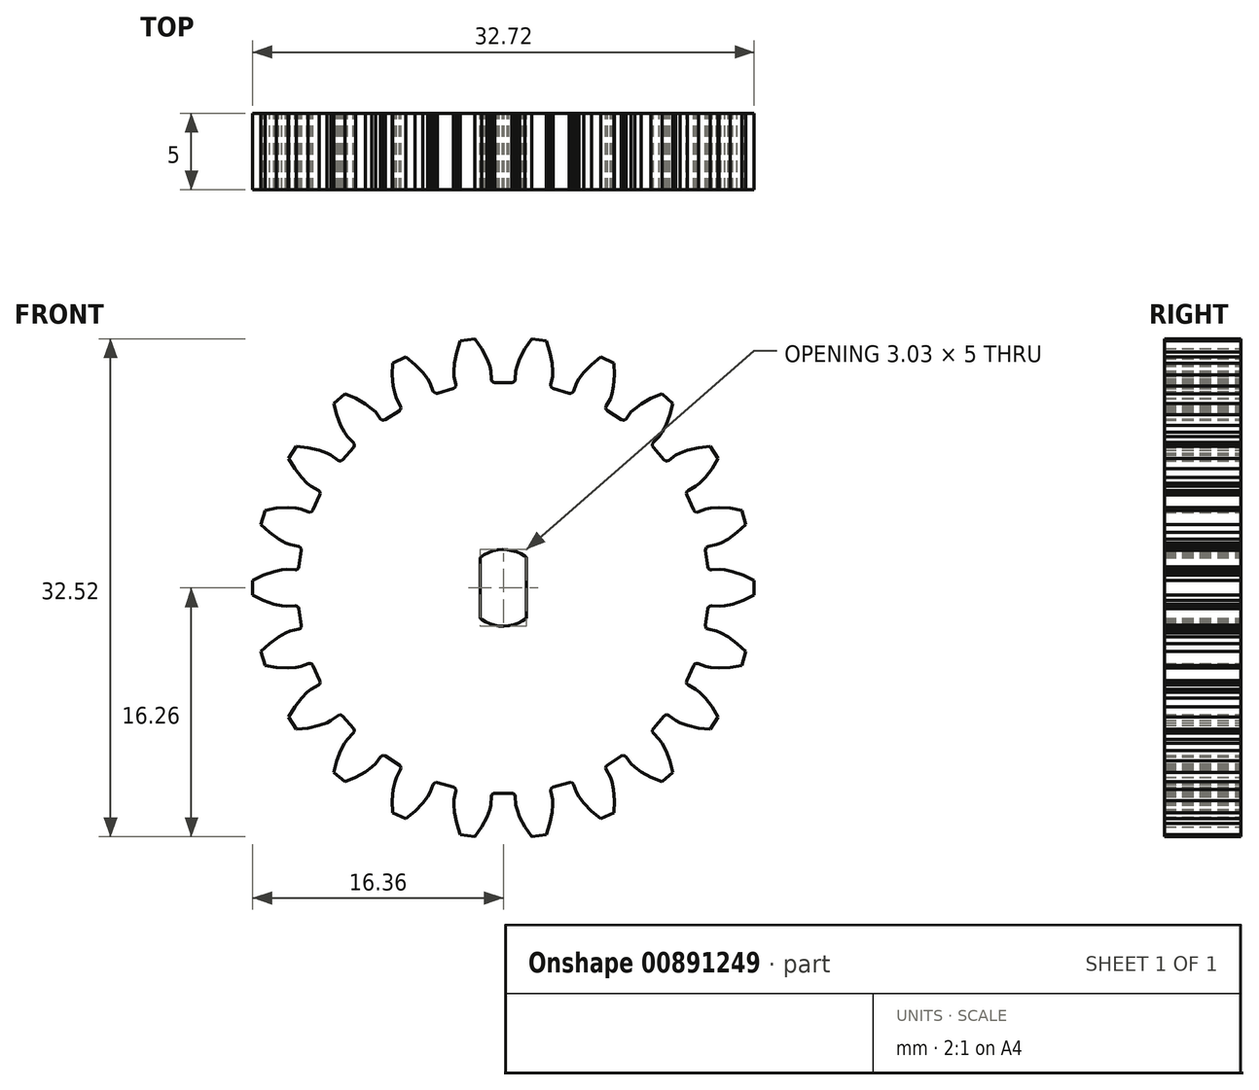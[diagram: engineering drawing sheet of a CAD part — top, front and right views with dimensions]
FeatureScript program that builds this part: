
annotation { "Feature Type Name" : "Feature", "Feature Type Description" : "" }
export const myFeature = defineFeature(function(context is Context, id is Id, definition is map)
    precondition{}
    {
        {
            var Q0;
            Q0=qCreatedBy(makeId("Front.planeOp"),FACE);
            var sketch = newSketch(context, id + "F0", { "sketchPlane" : qUnion([Q0])});
            skLineSegment(sketch, "E0", {"start": v(3.19, -14.67) * mm, "end": v(3.23, -14.15) * mm});
            skLineSegment(sketch, "E1", {"start": v(1.85, 16.26) * mm, "end": v(1.42, 15.62) * mm});
            skLineSegment(sketch, "E2", {"start": v(0.97, -2.3) * mm, "end": v(0.68, -2.4) * mm});
            skLineSegment(sketch, "E3", {"start": v(3.1, 13.28) * mm, "end": v(3.22, 13.83) * mm});
            skLineSegment(sketch, "E4", {"start": v(5.25, 14.06) * mm, "end": v(4.93, 13.65) * mm});
            skLineSegment(sketch, "E5", {"start": v(-9, -12.02) * mm, "end": v(-8.58, -11.7) * mm});
            skLineSegment(sketch, "E6", {"start": v(6.8, -11.58) * mm, "end": v(7.7, -10.99) * mm});
            skLineSegment(sketch, "E7", {"start": v(14.2, -2.94) * mm, "end": v(13.92, -2.82) * mm});
            skLineSegment(sketch, "E8", {"start": v(-0.54, 13.41) * mm, "end": v(-0.65, 13.44) * mm});
            skLineSegment(sketch, "E9", {"start": v(0.54, 13.41) * mm, "end": v(-0.54, 13.41) * mm});
            skLineSegment(sketch, "E10", {"start": v(-0.81, 14.18) * mm, "end": v(-0.89, 14.48) * mm});
            skLineSegment(sketch, "E11", {"start": v(-0.65, 13.44) * mm, "end": v(-0.74, 13.5) * mm});
            skLineSegment(sketch, "E12", {"start": v(-6.71, 11.66) * mm, "end": v(-6.8, 11.58) * mm});
            skLineSegment(sketch, "E13", {"start": v(0.81, 14.18) * mm, "end": v(0.77, 13.61) * mm});
            skLineSegment(sketch, "E14", {"start": v(-9.73, -9.3) * mm, "end": v(-9.73, -9.4) * mm});
            skLineSegment(sketch, "E15", {"start": v(3.1, 13.17) * mm, "end": v(3.1, 13.28) * mm});
            skLineSegment(sketch, "E16", {"start": v(-0.37, 2.47) * mm, "end": v(-0.06, 2.5) * mm});
            skLineSegment(sketch, "E17", {"start": v(0.68, -2.4) * mm, "end": v(0.37, -2.47) * mm});
            skLineSegment(sketch, "E18", {"start": v(4.57, 12.85) * mm, "end": v(4.51, 12.75) * mm});
            skLineSegment(sketch, "E19", {"start": v(0.89, 14.48) * mm, "end": v(0.81, 14.18) * mm});
            skLineSegment(sketch, "E20", {"start": v(1.25, -2.16) * mm, "end": v(0.97, -2.3) * mm});
            skLineSegment(sketch, "E21", {"start": v(-7.23, -14.68) * mm, "end": v(-6.36, -15.08) * mm});
            skLineSegment(sketch, "E22", {"start": v(-8.58, -11.7) * mm, "end": v(-8.35, -11.49) * mm});
            skLineSegment(sketch, "E23", {"start": v(-1.42, 15.62) * mm, "end": v(-1.85, 16.26) * mm});
            skLineSegment(sketch, "E24", {"start": v(0.37, -2.47) * mm, "end": v(0.06, -2.5) * mm});
            skLineSegment(sketch, "E25", {"start": v(-5.25, -14.06) * mm, "end": v(-4.93, -13.65) * mm});
            skLineSegment(sketch, "E26", {"start": v(3.04, 15.4) * mm, "end": v(2.8, 16.12) * mm});
            skLineSegment(sketch, "E27", {"start": v(-0.74, 13.5) * mm, "end": v(-0.77, 13.61) * mm});
            skLineSegment(sketch, "E28", {"start": v(14.07, -5.24) * mm, "end": v(14.8, -5.2) * mm});
            skLineSegment(sketch, "E29", {"start": v(-4.51, -12.75) * mm, "end": v(-4.41, -12.7) * mm});
            skLineSegment(sketch, "E30", {"start": v(-12.06, -6.36) * mm, "end": v(-12.56, -6.63) * mm});
            skLineSegment(sketch, "E31", {"start": v(-13.4, 1.27) * mm, "end": v(-13.48, 1.2) * mm});
            skLineSegment(sketch, "E32", {"start": v(-0.77, 13.61) * mm, "end": v(-0.81, 14.18) * mm});
            skLineSegment(sketch, "E33", {"start": v(-1.08, 14.97) * mm, "end": v(-1.42, 15.62) * mm});
            skLineSegment(sketch, "E34", {"start": v(-8, -11.04) * mm, "end": v(-7.92, -10.97) * mm});
            skLineSegment(sketch, "E35", {"start": v(-6.8, -11.58) * mm, "end": v(-6.71, -11.66) * mm});
            skLineSegment(sketch, "E36", {"start": v(-14.67, 3.2) * mm, "end": v(-14.2, 2.94) * mm});
            skLineSegment(sketch, "E37", {"start": v(-3.19, -14.67) * mm, "end": v(-3.04, -15.4) * mm});
            skLineSegment(sketch, "E38", {"start": v(0.54, -13.41) * mm, "end": v(0.65, -13.44) * mm});
            skLineSegment(sketch, "E39", {"start": v(-15.26, 3.63) * mm, "end": v(-14.67, 3.2) * mm});
            skLineSegment(sketch, "E40", {"start": v(-13.23, 5.15) * mm, "end": v(-13.54, 5.2) * mm});
            skLineSegment(sketch, "E41", {"start": v(-4.93, -13.65) * mm, "end": v(-4.77, -13.37) * mm});
            skLineSegment(sketch, "E42", {"start": v(-12.06, 6.36) * mm, "end": v(-11.98, 6.28) * mm});
            skLineSegment(sketch, "E43", {"start": v(-16.36, 0.48) * mm, "end": v(-16.36, -0.48) * mm});
            skLineSegment(sketch, "E44", {"start": v(-15.67, 0.82) * mm, "end": v(-16.36, 0.48) * mm});
            skLineSegment(sketch, "E45", {"start": v(3.19, 14.67) * mm, "end": v(3.04, 15.4) * mm});
            skLineSegment(sketch, "E46", {"start": v(3.23, 14.15) * mm, "end": v(3.19, 14.67) * mm});
            skLineSegment(sketch, "E47", {"start": v(3.22, 13.83) * mm, "end": v(3.23, 14.15) * mm});
            skLineSegment(sketch, "E48", {"start": v(0.26, 2.49) * mm, "end": v(0.57, 2.43) * mm});
            skLineSegment(sketch, "E49", {"start": v(-0.06, 2.5) * mm, "end": v(0.26, 2.49) * mm});
            skLineSegment(sketch, "E50", {"start": v(-14.02, -8.44) * mm, "end": v(-13.5, -9.25) * mm});
            skLineSegment(sketch, "E51", {"start": v(-13.62, -7.78) * mm, "end": v(-14.02, -8.44) * mm});
            skLineSegment(sketch, "E52", {"start": v(-0.68, 2.4) * mm, "end": v(-0.37, 2.47) * mm});
            skLineSegment(sketch, "E53", {"start": v(-3.16, 13.08) * mm, "end": v(-3.26, 13.02) * mm});
            skLineSegment(sketch, "E54", {"start": v(-3.1, 13.17) * mm, "end": v(-3.16, 13.08) * mm});
            skLineSegment(sketch, "E55", {"start": v(-3.1, 13.28) * mm, "end": v(-3.1, 13.17) * mm});
            skLineSegment(sketch, "E56", {"start": v(-3.22, 13.83) * mm, "end": v(-3.1, 13.28) * mm});
            skLineSegment(sketch, "E57", {"start": v(-3.23, 14.15) * mm, "end": v(-3.22, 13.83) * mm});
            skLineSegment(sketch, "E58", {"start": v(-3.19, 14.67) * mm, "end": v(-3.23, 14.15) * mm});
            skLineSegment(sketch, "E59", {"start": v(-3.04, 15.4) * mm, "end": v(-3.19, 14.67) * mm});
            skLineSegment(sketch, "E60", {"start": v(-2.8, 16.12) * mm, "end": v(-3.04, 15.4) * mm});
            skLineSegment(sketch, "E61", {"start": v(-1.85, 16.26) * mm, "end": v(-2.8, 16.12) * mm});
            skLineSegment(sketch, "E62", {"start": v(5.76, 14.6) * mm, "end": v(5.25, 14.06) * mm});
            skLineSegment(sketch, "E63", {"start": v(6.36, 15.08) * mm, "end": v(5.76, 14.6) * mm});
            skLineSegment(sketch, "E64", {"start": v(7.23, 14.68) * mm, "end": v(6.36, 15.08) * mm});
            skLineSegment(sketch, "E65", {"start": v(-7.2, 13.18) * mm, "end": v(-7.08, 12.66) * mm});
            skLineSegment(sketch, "E66", {"start": v(-7.25, 13.91) * mm, "end": v(-7.2, 13.18) * mm});
            skLineSegment(sketch, "E67", {"start": v(-7.23, 14.68) * mm, "end": v(-7.25, 13.91) * mm});
            skLineSegment(sketch, "E68", {"start": v(-6.36, 15.08) * mm, "end": v(-7.23, 14.68) * mm});
            skLineSegment(sketch, "E69", {"start": v(-5.76, 14.6) * mm, "end": v(-6.36, 15.08) * mm});
            skLineSegment(sketch, "E70", {"start": v(-5.25, 14.06) * mm, "end": v(-5.76, 14.6) * mm});
            skLineSegment(sketch, "E71", {"start": v(-4.93, 13.65) * mm, "end": v(-5.25, 14.06) * mm});
            skLineSegment(sketch, "E72", {"start": v(-4.77, 13.37) * mm, "end": v(-4.93, 13.65) * mm});
            skLineSegment(sketch, "E73", {"start": v(-4.57, 12.85) * mm, "end": v(-4.77, 13.37) * mm});
            skLineSegment(sketch, "E74", {"start": v(-4.51, 12.75) * mm, "end": v(-4.57, 12.85) * mm});
            skLineSegment(sketch, "E75", {"start": v(1.42, 15.62) * mm, "end": v(1.08, 14.97) * mm});
            skLineSegment(sketch, "E76", {"start": v(-13.54, 5.2) * mm, "end": v(-14.07, 5.24) * mm});
            skLineSegment(sketch, "E77", {"start": v(-0.89, 14.48) * mm, "end": v(-1.08, 14.97) * mm});
            skLineSegment(sketch, "E78", {"start": v(13.17, -7.2) * mm, "end": v(12.8, -6.82) * mm});
            skLineSegment(sketch, "E79", {"start": v(2.8, 16.12) * mm, "end": v(1.85, 16.26) * mm});
            skLineSegment(sketch, "E80", {"start": v(-2.8, -16.12) * mm, "end": v(-1.85, -16.26) * mm});
            skLineSegment(sketch, "E81", {"start": v(-11.97, -6.07) * mm, "end": v(-11.95, -6.17) * mm});
            skLineSegment(sketch, "E82", {"start": v(-6.71, -11.87) * mm, "end": v(-6.98, -12.36) * mm});
            skLineSegment(sketch, "E83", {"start": v(-14.46, 1.18) * mm, "end": v(-14.97, 1.07) * mm});
            skLineSegment(sketch, "E84", {"start": v(-14.07, 5.24) * mm, "end": v(-14.8, 5.2) * mm});
            skLineSegment(sketch, "E85", {"start": v(-1.85, -16.26) * mm, "end": v(-1.42, -15.62) * mm});
            skLineSegment(sketch, "E86", {"start": v(-6.36, -15.08) * mm, "end": v(-5.76, -14.6) * mm});
            skLineSegment(sketch, "E87", {"start": v(-4.3, -12.72) * mm, "end": v(-4.41, -12.7) * mm});
            skLineSegment(sketch, "E88", {"start": v(-7.7, -10.99) * mm, "end": v(-7.81, -10.95) * mm});
            skLineSegment(sketch, "E89", {"start": v(7.23, 14.68) * mm, "end": v(7.25, 13.91) * mm});
            skLineSegment(sketch, "E90", {"start": v(0.74, -13.5) * mm, "end": v(0.77, -13.61) * mm});
            skLineSegment(sketch, "E91", {"start": v(-15.56, 5.07) * mm, "end": v(-14.8, 5.2) * mm});
            skLineSegment(sketch, "E92", {"start": v(-3.22, -13.83) * mm, "end": v(-3.23, -14.15) * mm});
            skLineSegment(sketch, "E93", {"start": v(-15.56, 5.07) * mm, "end": v(-15.83, 4.15) * mm});
            skLineSegment(sketch, "E94", {"start": v(-12.8, -6.82) * mm, "end": v(-13.17, -7.2) * mm});
            skLineSegment(sketch, "E95", {"start": v(-13.23, 5.15) * mm, "end": v(-12.7, 4.96) * mm});
            skLineSegment(sketch, "E96", {"start": v(-5.25, -14.06) * mm, "end": v(-5.76, -14.6) * mm});
            skLineSegment(sketch, "E97", {"start": v(-15.26, 3.63) * mm, "end": v(-15.83, 4.15) * mm});
            skLineSegment(sketch, "E98", {"start": v(13.5, -9.25) * mm, "end": v(12.74, -9.16) * mm});
            skLineSegment(sketch, "E99", {"start": v(-13.2, -2.56) * mm, "end": v(-13.27, -2.65) * mm});
            skLineSegment(sketch, "E100", {"start": v(-12.8, -6.82) * mm, "end": v(-12.56, -6.63) * mm});
            skLineSegment(sketch, "E101", {"start": v(-13.48, -1.2) * mm, "end": v(-13.59, -1.18) * mm});
            skLineSegment(sketch, "E102", {"start": v(-3.16, -13.08) * mm, "end": v(-3.1, -13.17) * mm});
            skLineSegment(sketch, "E103", {"start": v(-0.89, -14.48) * mm, "end": v(-1.08, -14.97) * mm});
            skLineSegment(sketch, "E104", {"start": v(11.53, -8.81) * mm, "end": v(11.24, -8.67) * mm});
            skLineSegment(sketch, "E105", {"start": v(-12.02, -9) * mm, "end": v(-12.74, -9.16) * mm});
            skLineSegment(sketch, "E106", {"start": v(-7.81, -10.95) * mm, "end": v(-7.92, -10.97) * mm});
            skLineSegment(sketch, "E107", {"start": v(-0.54, -13.41) * mm, "end": v(-0.65, -13.44) * mm});
            skLineSegment(sketch, "E108", {"start": v(9.64, -12.38) * mm, "end": v(9, -12.02) * mm});
            skLineSegment(sketch, "E109", {"start": v(-3.1, -13.28) * mm, "end": v(-3.22, -13.83) * mm});
            skLineSegment(sketch, "E110", {"start": v(-3.04, -15.4) * mm, "end": v(-2.8, -16.12) * mm});
            skLineSegment(sketch, "E111", {"start": v(-1.5, -2) * mm, "end": v(-1.51, 1.99) * mm});
            skLineSegment(sketch, "E112", {"start": v(-1.42, -2.05) * mm, "end": v(-1.5, -2) * mm});
            skLineSegment(sketch, "E113", {"start": v(-1.16, -2.22) * mm, "end": v(-1.42, -2.05) * mm});
            skLineSegment(sketch, "E114", {"start": v(-1.42, -15.62) * mm, "end": v(-1.08, -14.97) * mm});
            skLineSegment(sketch, "E115", {"start": v(-0.87, -2.34) * mm, "end": v(-1.16, -2.22) * mm});
            skLineSegment(sketch, "E116", {"start": v(-0.89, -14.48) * mm, "end": v(-0.81, -14.18) * mm});
            skLineSegment(sketch, "E117", {"start": v(-0.57, -2.43) * mm, "end": v(-0.87, -2.34) * mm});
            skLineSegment(sketch, "E118", {"start": v(-0.81, -14.18) * mm, "end": v(-0.77, -13.61) * mm});
            skLineSegment(sketch, "E119", {"start": v(-0.77, -13.61) * mm, "end": v(-0.74, -13.5) * mm});
            skLineSegment(sketch, "E120", {"start": v(-0.74, -13.5) * mm, "end": v(-0.65, -13.44) * mm});
            skLineSegment(sketch, "E121", {"start": v(-0.26, -2.49) * mm, "end": v(-0.57, -2.43) * mm});
            skLineSegment(sketch, "E122", {"start": v(-0.54, -13.41) * mm, "end": v(0.54, -13.41) * mm});
            skLineSegment(sketch, "E123", {"start": v(0.06, -2.5) * mm, "end": v(-0.26, -2.49) * mm});
            skLineSegment(sketch, "E124", {"start": v(0.65, -13.44) * mm, "end": v(0.74, -13.5) * mm});
            skLineSegment(sketch, "E125", {"start": v(0.77, -13.61) * mm, "end": v(0.81, -14.18) * mm});
            skLineSegment(sketch, "E126", {"start": v(0.81, -14.18) * mm, "end": v(0.89, -14.48) * mm});
            skLineSegment(sketch, "E127", {"start": v(0.89, -14.48) * mm, "end": v(1.08, -14.97) * mm});
            skLineSegment(sketch, "E128", {"start": v(1.08, -14.97) * mm, "end": v(1.42, -15.62) * mm});
            skLineSegment(sketch, "E129", {"start": v(1.51, -1.99) * mm, "end": v(1.25, -2.16) * mm});
            skLineSegment(sketch, "E130", {"start": v(1.42, -15.62) * mm, "end": v(1.85, -16.26) * mm});
            skLineSegment(sketch, "E131", {"start": v(-15.26, -3.63) * mm, "end": v(-15.83, -4.15) * mm});
            skLineSegment(sketch, "E132", {"start": v(-15.83, -4.15) * mm, "end": v(-15.56, -5.07) * mm});
            skLineSegment(sketch, "E133", {"start": v(-15.56, -5.07) * mm, "end": v(-14.8, -5.2) * mm});
            skLineSegment(sketch, "E134", {"start": v(-14.67, -3.2) * mm, "end": v(-15.26, -3.63) * mm});
            skLineSegment(sketch, "E135", {"start": v(-14.8, -5.2) * mm, "end": v(-14.07, -5.24) * mm});
            skLineSegment(sketch, "E136", {"start": v(-14.2, -2.94) * mm, "end": v(-14.67, -3.2) * mm});
            skLineSegment(sketch, "E137", {"start": v(-13.92, -2.82) * mm, "end": v(-14.2, -2.94) * mm});
            skLineSegment(sketch, "E138", {"start": v(-14.07, -5.24) * mm, "end": v(-13.54, -5.2) * mm});
            skLineSegment(sketch, "E139", {"start": v(-13.37, -2.7) * mm, "end": v(-13.92, -2.82) * mm});
            skLineSegment(sketch, "E140", {"start": v(-13.54, -5.2) * mm, "end": v(-13.23, -5.15) * mm});
            skLineSegment(sketch, "E141", {"start": v(-13.27, -2.65) * mm, "end": v(-13.37, -2.7) * mm});
            skLineSegment(sketch, "E142", {"start": v(-13.23, -5.15) * mm, "end": v(-12.7, -4.96) * mm});
            skLineSegment(sketch, "E143", {"start": v(-13.2, -2.45) * mm, "end": v(-13.2, -2.56) * mm});
            skLineSegment(sketch, "E144", {"start": v(-13.17, -7.2) * mm, "end": v(-13.62, -7.78) * mm});
            skLineSegment(sketch, "E145", {"start": v(-13.5, -9.25) * mm, "end": v(-12.74, -9.16) * mm});
            skLineSegment(sketch, "E146", {"start": v(-11.98, -6.28) * mm, "end": v(-12.06, -6.36) * mm});
            skLineSegment(sketch, "E147", {"start": v(-12.02, -9) * mm, "end": v(-11.53, -8.81) * mm});
            skLineSegment(sketch, "E148", {"start": v(-11.95, -6.17) * mm, "end": v(-11.98, -6.28) * mm});
            skLineSegment(sketch, "E149", {"start": v(-10.88, -11.3) * mm, "end": v(-11.08, -12.05) * mm});
            skLineSegment(sketch, "E150", {"start": v(-11.08, -12.05) * mm, "end": v(-10.35, -12.68) * mm});
            skLineSegment(sketch, "E151", {"start": v(-10.61, -10.62) * mm, "end": v(-10.88, -11.3) * mm});
            skLineSegment(sketch, "E152", {"start": v(-10.36, -10.15) * mm, "end": v(-10.61, -10.62) * mm});
            skLineSegment(sketch, "E153", {"start": v(-10.18, -9.9) * mm, "end": v(-10.36, -10.15) * mm});
            skLineSegment(sketch, "E154", {"start": v(-10.35, -12.68) * mm, "end": v(-9.64, -12.38) * mm});
            skLineSegment(sketch, "E155", {"start": v(-9.79, -9.5) * mm, "end": v(-10.18, -9.9) * mm});
            skLineSegment(sketch, "E156", {"start": v(-9.73, -9.4) * mm, "end": v(-9.79, -9.5) * mm});
            skLineSegment(sketch, "E157", {"start": v(-7.2, -13.18) * mm, "end": v(-7.25, -13.91) * mm});
            skLineSegment(sketch, "E158", {"start": v(-7.25, -13.91) * mm, "end": v(-7.23, -14.68) * mm});
            skLineSegment(sketch, "E159", {"start": v(-7.08, -12.66) * mm, "end": v(-7.2, -13.18) * mm});
            skLineSegment(sketch, "E160", {"start": v(-6.98, -12.36) * mm, "end": v(-7.08, -12.66) * mm});
            skLineSegment(sketch, "E161", {"start": v(-6.69, -11.76) * mm, "end": v(-6.71, -11.87) * mm});
            skLineSegment(sketch, "E162", {"start": v(-3.23, -14.15) * mm, "end": v(-3.19, -14.67) * mm});
            skLineSegment(sketch, "E163", {"start": v(-7.08, 12.66) * mm, "end": v(-6.98, 12.36) * mm});
            skLineSegment(sketch, "E164", {"start": v(-6.98, 12.36) * mm, "end": v(-6.71, 11.87) * mm});
            skLineSegment(sketch, "E165", {"start": v(-6.71, 11.87) * mm, "end": v(-6.69, 11.76) * mm});
            skLineSegment(sketch, "E166", {"start": v(-4.77, -13.37) * mm, "end": v(-4.57, -12.85) * mm});
            skLineSegment(sketch, "E167", {"start": v(-4.57, -12.85) * mm, "end": v(-4.51, -12.75) * mm});
            skLineSegment(sketch, "E168", {"start": v(-4.41, 12.7) * mm, "end": v(-4.51, 12.75) * mm});
            skLineSegment(sketch, "E169", {"start": v(-4.3, 12.72) * mm, "end": v(-4.41, 12.7) * mm});
            skLineSegment(sketch, "E170", {"start": v(-4.3, -12.72) * mm, "end": v(-3.26, -13.02) * mm});
            skLineSegment(sketch, "E171", {"start": v(-3.26, 13.02) * mm, "end": v(-4.3, 12.72) * mm});
            skLineSegment(sketch, "E172", {"start": v(-3.26, -13.02) * mm, "end": v(-3.16, -13.08) * mm});
            skLineSegment(sketch, "E173", {"start": v(-3.1, -13.17) * mm, "end": v(-3.1, -13.28) * mm});
            skLineSegment(sketch, "E174", {"start": v(-10.35, 12.68) * mm, "end": v(-11.08, 12.05) * mm});
            skLineSegment(sketch, "E175", {"start": v(-11.08, 12.05) * mm, "end": v(-10.88, 11.3) * mm});
            skLineSegment(sketch, "E176", {"start": v(-10.88, 11.3) * mm, "end": v(-10.61, 10.62) * mm});
            skLineSegment(sketch, "E177", {"start": v(-10.61, 10.62) * mm, "end": v(-10.36, 10.15) * mm});
            skLineSegment(sketch, "E178", {"start": v(-10.36, 10.15) * mm, "end": v(-10.18, 9.9) * mm});
            skLineSegment(sketch, "E179", {"start": v(-9.64, 12.38) * mm, "end": v(-10.35, 12.68) * mm});
            skLineSegment(sketch, "E180", {"start": v(-10.18, 9.9) * mm, "end": v(-9.79, 9.5) * mm});
            skLineSegment(sketch, "E181", {"start": v(-9.79, 9.5) * mm, "end": v(-9.73, 9.4) * mm});
            skLineSegment(sketch, "E182", {"start": v(-9.73, 9.4) * mm, "end": v(-9.73, 9.3) * mm});
            skLineSegment(sketch, "E183", {"start": v(-9.64, -12.38) * mm, "end": v(-9, -12.02) * mm});
            skLineSegment(sketch, "E184", {"start": v(-9, 12.02) * mm, "end": v(-9.64, 12.38) * mm});
            skLineSegment(sketch, "E185", {"start": v(-8.58, 11.7) * mm, "end": v(-9, 12.02) * mm});
            skLineSegment(sketch, "E186", {"start": v(-8.35, 11.49) * mm, "end": v(-8.58, 11.7) * mm});
            skLineSegment(sketch, "E187", {"start": v(-8.35, -11.49) * mm, "end": v(-8, -11.04) * mm});
            skLineSegment(sketch, "E188", {"start": v(-8, 11.04) * mm, "end": v(-8.35, 11.49) * mm});
            skLineSegment(sketch, "E189", {"start": v(-7.92, 10.97) * mm, "end": v(-8, 11.04) * mm});
            skLineSegment(sketch, "E190", {"start": v(-7.81, 10.95) * mm, "end": v(-7.92, 10.97) * mm});
            skLineSegment(sketch, "E191", {"start": v(-7.7, 10.99) * mm, "end": v(-7.81, 10.95) * mm});
            skLineSegment(sketch, "E192", {"start": v(-7.7, -10.99) * mm, "end": v(-6.8, -11.58) * mm});
            skLineSegment(sketch, "E193", {"start": v(-6.8, 11.58) * mm, "end": v(-7.7, 10.99) * mm});
            skLineSegment(sketch, "E194", {"start": v(-6.71, -11.66) * mm, "end": v(-6.69, -11.76) * mm});
            skLineSegment(sketch, "E195", {"start": v(-6.69, 11.76) * mm, "end": v(-6.71, 11.66) * mm});
            skLineSegment(sketch, "E196", {"start": v(-13.5, 9.25) * mm, "end": v(-14.02, 8.44) * mm});
            skLineSegment(sketch, "E197", {"start": v(-14.02, 8.44) * mm, "end": v(-13.62, 7.78) * mm});
            skLineSegment(sketch, "E198", {"start": v(-13.62, 7.78) * mm, "end": v(-13.17, 7.2) * mm});
            skLineSegment(sketch, "E199", {"start": v(-12.74, 9.16) * mm, "end": v(-13.5, 9.25) * mm});
            skLineSegment(sketch, "E200", {"start": v(-13.17, 7.2) * mm, "end": v(-12.8, 6.82) * mm});
            skLineSegment(sketch, "E201", {"start": v(-12.8, 6.82) * mm, "end": v(-12.56, 6.63) * mm});
            skLineSegment(sketch, "E202", {"start": v(-12.02, 9) * mm, "end": v(-12.74, 9.16) * mm});
            skLineSegment(sketch, "E203", {"start": v(-12.56, 6.63) * mm, "end": v(-12.06, 6.36) * mm});
            skLineSegment(sketch, "E204", {"start": v(-11.53, 8.81) * mm, "end": v(-12.02, 9) * mm});
            skLineSegment(sketch, "E205", {"start": v(-11.98, 6.28) * mm, "end": v(-11.95, 6.17) * mm});
            skLineSegment(sketch, "E206", {"start": v(-11.53, -8.81) * mm, "end": v(-11.24, -8.67) * mm});
            skLineSegment(sketch, "E207", {"start": v(-11.24, 8.67) * mm, "end": v(-11.53, 8.81) * mm});
            skLineSegment(sketch, "E208", {"start": v(-11.24, -8.67) * mm, "end": v(-10.8, -8.33) * mm});
            skLineSegment(sketch, "E209", {"start": v(-10.8, 8.33) * mm, "end": v(-11.24, 8.67) * mm});
            skLineSegment(sketch, "E210", {"start": v(-10.8, -8.33) * mm, "end": v(-10.7, -8.3) * mm});
            skLineSegment(sketch, "E211", {"start": v(-10.7, 8.3) * mm, "end": v(-10.8, 8.33) * mm});
            skLineSegment(sketch, "E212", {"start": v(-10.7, -8.3) * mm, "end": v(-10.58, -8.3) * mm});
            skLineSegment(sketch, "E213", {"start": v(-10.58, 8.3) * mm, "end": v(-10.7, 8.3) * mm});
            skLineSegment(sketch, "E214", {"start": v(-10.58, -8.3) * mm, "end": v(-10.5, -8.37) * mm});
            skLineSegment(sketch, "E215", {"start": v(-10.5, 8.37) * mm, "end": v(-10.58, 8.3) * mm});
            skLineSegment(sketch, "E216", {"start": v(-10.5, -8.37) * mm, "end": v(-9.78, -9.2) * mm});
            skLineSegment(sketch, "E217", {"start": v(-9.78, 9.2) * mm, "end": v(-10.5, 8.37) * mm});
            skLineSegment(sketch, "E218", {"start": v(-9.78, -9.2) * mm, "end": v(-9.73, -9.3) * mm});
            skLineSegment(sketch, "E219", {"start": v(-9.73, 9.3) * mm, "end": v(-9.78, 9.2) * mm});
            skLineSegment(sketch, "E220", {"start": v(-14.2, 2.94) * mm, "end": v(-13.92, 2.82) * mm});
            skLineSegment(sketch, "E221", {"start": v(-13.92, 2.82) * mm, "end": v(-13.37, 2.7) * mm});
            skLineSegment(sketch, "E222", {"start": v(-13.37, 2.7) * mm, "end": v(-13.27, 2.65) * mm});
            skLineSegment(sketch, "E223", {"start": v(-13.27, 2.65) * mm, "end": v(-13.2, 2.56) * mm});
            skLineSegment(sketch, "E224", {"start": v(-13.2, 2.56) * mm, "end": v(-13.2, 2.45) * mm});
            skLineSegment(sketch, "E225", {"start": v(-12.7, -4.96) * mm, "end": v(-12.6, -4.94) * mm});
            skLineSegment(sketch, "E226", {"start": v(-12.6, 4.94) * mm, "end": v(-12.7, 4.96) * mm});
            skLineSegment(sketch, "E227", {"start": v(-12.6, -4.94) * mm, "end": v(-12.5, -4.99) * mm});
            skLineSegment(sketch, "E228", {"start": v(-12.5, 4.99) * mm, "end": v(-12.6, 4.94) * mm});
            skLineSegment(sketch, "E229", {"start": v(-12.5, -4.99) * mm, "end": v(-12.43, -5.08) * mm});
            skLineSegment(sketch, "E230", {"start": v(-12.43, 5.08) * mm, "end": v(-12.5, 4.99) * mm});
            skLineSegment(sketch, "E231", {"start": v(-12.43, -5.08) * mm, "end": v(-11.97, -6.07) * mm});
            skLineSegment(sketch, "E232", {"start": v(-11.97, 6.07) * mm, "end": v(-12.43, 5.08) * mm});
            skLineSegment(sketch, "E233", {"start": v(-11.95, 6.17) * mm, "end": v(-11.97, 6.07) * mm});
            skLineSegment(sketch, "E234", {"start": v(-16.36, -0.48) * mm, "end": v(-15.67, -0.82) * mm});
            skLineSegment(sketch, "E235", {"start": v(-15.67, -0.82) * mm, "end": v(-14.97, -1.07) * mm});
            skLineSegment(sketch, "E236", {"start": v(-14.97, 1.07) * mm, "end": v(-15.67, 0.82) * mm});
            skLineSegment(sketch, "E237", {"start": v(-14.97, -1.07) * mm, "end": v(-14.46, -1.18) * mm});
            skLineSegment(sketch, "E238", {"start": v(-14.46, -1.18) * mm, "end": v(-14.15, -1.22) * mm});
            skLineSegment(sketch, "E239", {"start": v(-14.15, 1.22) * mm, "end": v(-14.46, 1.18) * mm});
            skLineSegment(sketch, "E240", {"start": v(-14.15, -1.22) * mm, "end": v(-13.59, -1.18) * mm});
            skLineSegment(sketch, "E241", {"start": v(-13.59, 1.18) * mm, "end": v(-14.15, 1.22) * mm});
            skLineSegment(sketch, "E242", {"start": v(-13.48, 1.2) * mm, "end": v(-13.59, 1.18) * mm});
            skLineSegment(sketch, "E243", {"start": v(-13.48, -1.2) * mm, "end": v(-13.4, -1.27) * mm});
            skLineSegment(sketch, "E244", {"start": v(-13.4, -1.27) * mm, "end": v(-13.35, -1.37) * mm});
            skLineSegment(sketch, "E245", {"start": v(-13.35, 1.37) * mm, "end": v(-13.4, 1.27) * mm});
            skLineSegment(sketch, "E246", {"start": v(-13.35, -1.37) * mm, "end": v(-13.2, -2.45) * mm});
            skLineSegment(sketch, "E247", {"start": v(-13.2, 2.45) * mm, "end": v(-13.35, 1.37) * mm});
            skLineSegment(sketch, "E248", {"start": v(-1.51, 1.99) * mm, "end": v(-1.25, 2.16) * mm});
            skLineSegment(sketch, "E249", {"start": v(-1.25, 2.16) * mm, "end": v(-0.97, 2.3) * mm});
            skLineSegment(sketch, "E250", {"start": v(-0.97, 2.3) * mm, "end": v(-0.68, 2.4) * mm});
            skLineSegment(sketch, "E251", {"start": v(0.65, 13.44) * mm, "end": v(0.54, 13.41) * mm});
            skLineSegment(sketch, "E252", {"start": v(0.57, 2.43) * mm, "end": v(0.87, 2.34) * mm});
            skLineSegment(sketch, "E253", {"start": v(0.74, 13.5) * mm, "end": v(0.65, 13.44) * mm});
            skLineSegment(sketch, "E254", {"start": v(0.77, 13.61) * mm, "end": v(0.74, 13.5) * mm});
            skLineSegment(sketch, "E255", {"start": v(0.87, 2.34) * mm, "end": v(1.16, 2.22) * mm});
            skLineSegment(sketch, "E256", {"start": v(1.08, 14.97) * mm, "end": v(0.89, 14.48) * mm});
            skLineSegment(sketch, "E257", {"start": v(1.16, 2.22) * mm, "end": v(1.42, 2.05) * mm});
            skLineSegment(sketch, "E258", {"start": v(1.42, 2.05) * mm, "end": v(1.5, 2) * mm});
            skLineSegment(sketch, "E259", {"start": v(1.5, 2) * mm, "end": v(1.51, -1.99) * mm});
            skLineSegment(sketch, "E260", {"start": v(1.85, -16.26) * mm, "end": v(2.8, -16.12) * mm});
            skLineSegment(sketch, "E261", {"start": v(2.8, -16.12) * mm, "end": v(3.04, -15.4) * mm});
            skLineSegment(sketch, "E262", {"start": v(3.04, -15.4) * mm, "end": v(3.19, -14.67) * mm});
            skLineSegment(sketch, "E263", {"start": v(3.22, -13.83) * mm, "end": v(3.1, -13.28) * mm});
            skLineSegment(sketch, "E264", {"start": v(3.23, -14.15) * mm, "end": v(3.22, -13.83) * mm});
            skLineSegment(sketch, "E265", {"start": v(3.1, -13.28) * mm, "end": v(3.1, -13.17) * mm});
            skLineSegment(sketch, "E266", {"start": v(3.1, -13.17) * mm, "end": v(3.16, -13.08) * mm});
            skLineSegment(sketch, "E267", {"start": v(3.16, 13.08) * mm, "end": v(3.1, 13.17) * mm});
            skLineSegment(sketch, "E268", {"start": v(3.16, -13.08) * mm, "end": v(3.26, -13.02) * mm});
            skLineSegment(sketch, "E269", {"start": v(3.26, 13.02) * mm, "end": v(3.16, 13.08) * mm});
            skLineSegment(sketch, "E270", {"start": v(3.26, -13.02) * mm, "end": v(4.3, -12.72) * mm});
            skLineSegment(sketch, "E271", {"start": v(4.3, 12.72) * mm, "end": v(3.26, 13.02) * mm});
            skLineSegment(sketch, "E272", {"start": v(4.3, -12.72) * mm, "end": v(4.41, -12.7) * mm});
            skLineSegment(sketch, "E273", {"start": v(4.41, 12.7) * mm, "end": v(4.3, 12.72) * mm});
            skLineSegment(sketch, "E274", {"start": v(4.41, -12.7) * mm, "end": v(4.51, -12.75) * mm});
            skLineSegment(sketch, "E275", {"start": v(4.51, 12.75) * mm, "end": v(4.41, 12.7) * mm});
            skLineSegment(sketch, "E276", {"start": v(4.51, -12.75) * mm, "end": v(4.57, -12.85) * mm});
            skLineSegment(sketch, "E277", {"start": v(4.57, -12.85) * mm, "end": v(4.77, -13.37) * mm});
            skLineSegment(sketch, "E278", {"start": v(4.77, 13.37) * mm, "end": v(4.57, 12.85) * mm});
            skLineSegment(sketch, "E279", {"start": v(4.77, -13.37) * mm, "end": v(4.93, -13.65) * mm});
            skLineSegment(sketch, "E280", {"start": v(4.93, 13.65) * mm, "end": v(4.77, 13.37) * mm});
            skLineSegment(sketch, "E281", {"start": v(4.93, -13.65) * mm, "end": v(5.25, -14.06) * mm});
            skLineSegment(sketch, "E282", {"start": v(5.25, -14.06) * mm, "end": v(5.76, -14.6) * mm});
            skLineSegment(sketch, "E283", {"start": v(5.76, -14.6) * mm, "end": v(6.36, -15.08) * mm});
            skLineSegment(sketch, "E284", {"start": v(6.36, -15.08) * mm, "end": v(7.23, -14.68) * mm});
            skLineSegment(sketch, "E285", {"start": v(6.71, -11.87) * mm, "end": v(6.69, -11.76) * mm});
            skLineSegment(sketch, "E286", {"start": v(6.98, -12.36) * mm, "end": v(6.71, -11.87) * mm});
            skLineSegment(sketch, "E287", {"start": v(7.08, -12.66) * mm, "end": v(6.98, -12.36) * mm});
            skLineSegment(sketch, "E288", {"start": v(7.2, -13.18) * mm, "end": v(7.08, -12.66) * mm});
            skLineSegment(sketch, "E289", {"start": v(7.23, -14.68) * mm, "end": v(7.25, -13.91) * mm});
            skLineSegment(sketch, "E290", {"start": v(7.25, -13.91) * mm, "end": v(7.2, -13.18) * mm});
            skLineSegment(sketch, "E291", {"start": v(6.69, -11.76) * mm, "end": v(6.71, -11.66) * mm});
            skLineSegment(sketch, "E292", {"start": v(6.71, 11.66) * mm, "end": v(6.69, 11.76) * mm});
            skLineSegment(sketch, "E293", {"start": v(6.71, -11.66) * mm, "end": v(6.8, -11.58) * mm});
            skLineSegment(sketch, "E294", {"start": v(6.8, 11.58) * mm, "end": v(6.71, 11.66) * mm});
            skLineSegment(sketch, "E295", {"start": v(7.7, 10.99) * mm, "end": v(6.8, 11.58) * mm});
            skLineSegment(sketch, "E296", {"start": v(7.7, -10.99) * mm, "end": v(7.81, -10.95) * mm});
            skLineSegment(sketch, "E297", {"start": v(7.81, 10.95) * mm, "end": v(7.7, 10.99) * mm});
            skLineSegment(sketch, "E298", {"start": v(7.81, -10.95) * mm, "end": v(7.92, -10.97) * mm});
            skLineSegment(sketch, "E299", {"start": v(7.92, 10.97) * mm, "end": v(7.81, 10.95) * mm});
            skLineSegment(sketch, "E300", {"start": v(7.92, -10.97) * mm, "end": v(8, -11.04) * mm});
            skLineSegment(sketch, "E301", {"start": v(8, 11.04) * mm, "end": v(7.92, 10.97) * mm});
            skLineSegment(sketch, "E302", {"start": v(8, -11.04) * mm, "end": v(8.35, -11.49) * mm});
            skLineSegment(sketch, "E303", {"start": v(8.35, 11.49) * mm, "end": v(8, 11.04) * mm});
            skLineSegment(sketch, "E304", {"start": v(8.35, -11.49) * mm, "end": v(8.58, -11.7) * mm});
            skLineSegment(sketch, "E305", {"start": v(8.58, 11.7) * mm, "end": v(8.35, 11.49) * mm});
            skLineSegment(sketch, "E306", {"start": v(8.58, -11.7) * mm, "end": v(9, -12.02) * mm});
            skLineSegment(sketch, "E307", {"start": v(9, 12.02) * mm, "end": v(8.58, 11.7) * mm});
            skLineSegment(sketch, "E308", {"start": v(9.64, 12.38) * mm, "end": v(9, 12.02) * mm});
            skLineSegment(sketch, "E309", {"start": v(9.73, -9.4) * mm, "end": v(9.73, -9.3) * mm});
            skLineSegment(sketch, "E310", {"start": v(9.64, -12.38) * mm, "end": v(10.35, -12.68) * mm});
            skLineSegment(sketch, "E311", {"start": v(9.79, -9.5) * mm, "end": v(9.73, -9.4) * mm});
            skLineSegment(sketch, "E312", {"start": v(10.18, -9.9) * mm, "end": v(9.79, -9.5) * mm});
            skLineSegment(sketch, "E313", {"start": v(10.36, -10.15) * mm, "end": v(10.18, -9.9) * mm});
            skLineSegment(sketch, "E314", {"start": v(10.35, -12.68) * mm, "end": v(11.08, -12.05) * mm});
            skLineSegment(sketch, "E315", {"start": v(10.61, -10.62) * mm, "end": v(10.36, -10.15) * mm});
            skLineSegment(sketch, "E316", {"start": v(11.08, -12.05) * mm, "end": v(10.88, -11.3) * mm});
            skLineSegment(sketch, "E317", {"start": v(10.88, -11.3) * mm, "end": v(10.61, -10.62) * mm});
            skLineSegment(sketch, "E318", {"start": v(9.73, -9.3) * mm, "end": v(9.78, -9.2) * mm});
            skLineSegment(sketch, "E319", {"start": v(9.78, 9.2) * mm, "end": v(9.73, 9.3) * mm});
            skLineSegment(sketch, "E320", {"start": v(9.78, -9.2) * mm, "end": v(10.5, -8.37) * mm});
            skLineSegment(sketch, "E321", {"start": v(10.5, 8.37) * mm, "end": v(9.78, 9.2) * mm});
            skLineSegment(sketch, "E322", {"start": v(10.5, -8.37) * mm, "end": v(10.58, -8.3) * mm});
            skLineSegment(sketch, "E323", {"start": v(10.58, 8.3) * mm, "end": v(10.5, 8.37) * mm});
            skLineSegment(sketch, "E324", {"start": v(10.58, -8.3) * mm, "end": v(10.7, -8.3) * mm});
            skLineSegment(sketch, "E325", {"start": v(10.7, 8.3) * mm, "end": v(10.58, 8.3) * mm});
            skLineSegment(sketch, "E326", {"start": v(10.7, -8.3) * mm, "end": v(10.8, -8.33) * mm});
            skLineSegment(sketch, "E327", {"start": v(10.8, 8.33) * mm, "end": v(10.7, 8.3) * mm});
            skLineSegment(sketch, "E328", {"start": v(10.8, -8.33) * mm, "end": v(11.24, -8.67) * mm});
            skLineSegment(sketch, "E329", {"start": v(11.24, 8.67) * mm, "end": v(10.8, 8.33) * mm});
            skLineSegment(sketch, "E330", {"start": v(11.53, 8.81) * mm, "end": v(11.24, 8.67) * mm});
            skLineSegment(sketch, "E331", {"start": v(11.53, -8.81) * mm, "end": v(12.02, -9) * mm});
            skLineSegment(sketch, "E332", {"start": v(11.98, -6.28) * mm, "end": v(11.95, -6.17) * mm});
            skLineSegment(sketch, "E333", {"start": v(12.06, -6.36) * mm, "end": v(11.98, -6.28) * mm});
            skLineSegment(sketch, "E334", {"start": v(12.02, -9) * mm, "end": v(12.74, -9.16) * mm});
            skLineSegment(sketch, "E335", {"start": v(12.56, -6.63) * mm, "end": v(12.06, -6.36) * mm});
            skLineSegment(sketch, "E336", {"start": v(12.8, -6.82) * mm, "end": v(12.56, -6.63) * mm});
            skLineSegment(sketch, "E337", {"start": v(13.62, -7.78) * mm, "end": v(13.17, -7.2) * mm});
            skLineSegment(sketch, "E338", {"start": v(13.5, -9.25) * mm, "end": v(14.02, -8.44) * mm});
            skLineSegment(sketch, "E339", {"start": v(14.02, -8.44) * mm, "end": v(13.62, -7.78) * mm});
            skLineSegment(sketch, "E340", {"start": v(11.95, -6.17) * mm, "end": v(11.97, -6.07) * mm});
            skLineSegment(sketch, "E341", {"start": v(11.97, 6.07) * mm, "end": v(11.95, 6.17) * mm});
            skLineSegment(sketch, "E342", {"start": v(11.97, -6.07) * mm, "end": v(12.43, -5.08) * mm});
            skLineSegment(sketch, "E343", {"start": v(12.43, 5.08) * mm, "end": v(11.97, 6.07) * mm});
            skLineSegment(sketch, "E344", {"start": v(12.43, -5.08) * mm, "end": v(12.5, -4.99) * mm});
            skLineSegment(sketch, "E345", {"start": v(12.5, 4.99) * mm, "end": v(12.43, 5.08) * mm});
            skLineSegment(sketch, "E346", {"start": v(12.5, -4.99) * mm, "end": v(12.6, -4.94) * mm});
            skLineSegment(sketch, "E347", {"start": v(12.6, 4.94) * mm, "end": v(12.5, 4.99) * mm});
            skLineSegment(sketch, "E348", {"start": v(12.6, -4.94) * mm, "end": v(12.7, -4.96) * mm});
            skLineSegment(sketch, "E349", {"start": v(12.7, 4.96) * mm, "end": v(12.6, 4.94) * mm});
            skLineSegment(sketch, "E350", {"start": v(12.7, -4.96) * mm, "end": v(13.23, -5.15) * mm});
            skLineSegment(sketch, "E351", {"start": v(13.2, -2.56) * mm, "end": v(13.2, -2.45) * mm});
            skLineSegment(sketch, "E352", {"start": v(13.27, -2.65) * mm, "end": v(13.2, -2.56) * mm});
            skLineSegment(sketch, "E353", {"start": v(13.23, -5.15) * mm, "end": v(13.54, -5.2) * mm});
            skLineSegment(sketch, "E354", {"start": v(13.37, -2.7) * mm, "end": v(13.27, -2.65) * mm});
            skLineSegment(sketch, "E355", {"start": v(13.92, -2.82) * mm, "end": v(13.37, -2.7) * mm});
            skLineSegment(sketch, "E356", {"start": v(13.54, -5.2) * mm, "end": v(14.07, -5.24) * mm});
            skLineSegment(sketch, "E357", {"start": v(14.67, -3.2) * mm, "end": v(14.2, -2.94) * mm});
            skLineSegment(sketch, "E358", {"start": v(15.26, -3.63) * mm, "end": v(14.67, -3.2) * mm});
            skLineSegment(sketch, "E359", {"start": v(14.8, -5.2) * mm, "end": v(15.56, -5.07) * mm});
            skLineSegment(sketch, "E360", {"start": v(15.56, -5.07) * mm, "end": v(15.83, -4.15) * mm});
            skLineSegment(sketch, "E361", {"start": v(15.83, -4.15) * mm, "end": v(15.26, -3.63) * mm});
            skLineSegment(sketch, "E362", {"start": v(13.2, -2.45) * mm, "end": v(13.35, -1.37) * mm});
            skLineSegment(sketch, "E363", {"start": v(13.35, 1.37) * mm, "end": v(13.2, 2.45) * mm});
            skLineSegment(sketch, "E364", {"start": v(13.35, -1.37) * mm, "end": v(13.4, -1.27) * mm});
            skLineSegment(sketch, "E365", {"start": v(13.4, 1.27) * mm, "end": v(13.35, 1.37) * mm});
            skLineSegment(sketch, "E366", {"start": v(13.4, -1.27) * mm, "end": v(13.48, -1.2) * mm});
            skLineSegment(sketch, "E367", {"start": v(13.48, 1.2) * mm, "end": v(13.4, 1.27) * mm});
            skLineSegment(sketch, "E368", {"start": v(13.59, 1.18) * mm, "end": v(13.48, 1.2) * mm});
            skLineSegment(sketch, "E369", {"start": v(13.48, -1.2) * mm, "end": v(13.59, -1.18) * mm});
            skLineSegment(sketch, "E370", {"start": v(13.59, -1.18) * mm, "end": v(14.15, -1.22) * mm});
            skLineSegment(sketch, "E371", {"start": v(14.15, 1.22) * mm, "end": v(13.59, 1.18) * mm});
            skLineSegment(sketch, "E372", {"start": v(14.46, 1.18) * mm, "end": v(14.15, 1.22) * mm});
            skLineSegment(sketch, "E373", {"start": v(14.15, -1.22) * mm, "end": v(14.46, -1.18) * mm});
            skLineSegment(sketch, "E374", {"start": v(14.46, -1.18) * mm, "end": v(14.97, -1.07) * mm});
            skLineSegment(sketch, "E375", {"start": v(14.97, 1.07) * mm, "end": v(14.46, 1.18) * mm});
            skLineSegment(sketch, "E376", {"start": v(14.97, -1.07) * mm, "end": v(15.67, -0.82) * mm});
            skLineSegment(sketch, "E377", {"start": v(15.67, 0.82) * mm, "end": v(14.97, 1.07) * mm});
            skLineSegment(sketch, "E378", {"start": v(15.67, -0.82) * mm, "end": v(16.36, -0.48) * mm});
            skLineSegment(sketch, "E379", {"start": v(16.36, -0.48) * mm, "end": v(16.36, 0.48) * mm});
            skLineSegment(sketch, "E380", {"start": v(16.36, 0.48) * mm, "end": v(15.67, 0.82) * mm});
            skLineSegment(sketch, "E381", {"start": v(13.23, 5.15) * mm, "end": v(12.7, 4.96) * mm});
            skLineSegment(sketch, "E382", {"start": v(13.2, 2.45) * mm, "end": v(13.2, 2.56) * mm});
            skLineSegment(sketch, "E383", {"start": v(13.2, 2.56) * mm, "end": v(13.27, 2.65) * mm});
            skLineSegment(sketch, "E384", {"start": v(13.54, 5.2) * mm, "end": v(13.23, 5.15) * mm});
            skLineSegment(sketch, "E385", {"start": v(13.27, 2.65) * mm, "end": v(13.37, 2.7) * mm});
            skLineSegment(sketch, "E386", {"start": v(13.37, 2.7) * mm, "end": v(13.92, 2.82) * mm});
            skLineSegment(sketch, "E387", {"start": v(14.07, 5.24) * mm, "end": v(13.54, 5.2) * mm});
            skLineSegment(sketch, "E388", {"start": v(13.92, 2.82) * mm, "end": v(14.2, 2.94) * mm});
            skLineSegment(sketch, "E389", {"start": v(14.8, 5.2) * mm, "end": v(14.07, 5.24) * mm});
            skLineSegment(sketch, "E390", {"start": v(14.2, 2.94) * mm, "end": v(14.67, 3.2) * mm});
            skLineSegment(sketch, "E391", {"start": v(14.67, 3.2) * mm, "end": v(15.26, 3.63) * mm});
            skLineSegment(sketch, "E392", {"start": v(15.56, 5.07) * mm, "end": v(14.8, 5.2) * mm});
            skLineSegment(sketch, "E393", {"start": v(15.26, 3.63) * mm, "end": v(15.83, 4.15) * mm});
            skLineSegment(sketch, "E394", {"start": v(15.83, 4.15) * mm, "end": v(15.56, 5.07) * mm});
            skLineSegment(sketch, "E395", {"start": v(12.02, 9) * mm, "end": v(11.53, 8.81) * mm});
            skLineSegment(sketch, "E396", {"start": v(11.95, 6.17) * mm, "end": v(11.98, 6.28) * mm});
            skLineSegment(sketch, "E397", {"start": v(11.98, 6.28) * mm, "end": v(12.06, 6.36) * mm});
            skLineSegment(sketch, "E398", {"start": v(12.74, 9.16) * mm, "end": v(12.02, 9) * mm});
            skLineSegment(sketch, "E399", {"start": v(12.06, 6.36) * mm, "end": v(12.56, 6.63) * mm});
            skLineSegment(sketch, "E400", {"start": v(12.56, 6.63) * mm, "end": v(12.8, 6.82) * mm});
            skLineSegment(sketch, "E401", {"start": v(13.5, 9.25) * mm, "end": v(12.74, 9.16) * mm});
            skLineSegment(sketch, "E402", {"start": v(12.8, 6.82) * mm, "end": v(13.17, 7.2) * mm});
            skLineSegment(sketch, "E403", {"start": v(13.17, 7.2) * mm, "end": v(13.62, 7.78) * mm});
            skLineSegment(sketch, "E404", {"start": v(13.62, 7.78) * mm, "end": v(14.02, 8.44) * mm});
            skLineSegment(sketch, "E405", {"start": v(14.02, 8.44) * mm, "end": v(13.5, 9.25) * mm});
            skLineSegment(sketch, "E406", {"start": v(10.35, 12.68) * mm, "end": v(9.64, 12.38) * mm});
            skLineSegment(sketch, "E407", {"start": v(9.73, 9.3) * mm, "end": v(9.73, 9.4) * mm});
            skLineSegment(sketch, "E408", {"start": v(9.73, 9.4) * mm, "end": v(9.79, 9.5) * mm});
            skLineSegment(sketch, "E409", {"start": v(9.79, 9.5) * mm, "end": v(10.18, 9.9) * mm});
            skLineSegment(sketch, "E410", {"start": v(10.18, 9.9) * mm, "end": v(10.36, 10.15) * mm});
            skLineSegment(sketch, "E411", {"start": v(11.08, 12.05) * mm, "end": v(10.35, 12.68) * mm});
            skLineSegment(sketch, "E412", {"start": v(10.36, 10.15) * mm, "end": v(10.61, 10.62) * mm});
            skLineSegment(sketch, "E413", {"start": v(10.61, 10.62) * mm, "end": v(10.88, 11.3) * mm});
            skLineSegment(sketch, "E414", {"start": v(10.88, 11.3) * mm, "end": v(11.08, 12.05) * mm});
            skLineSegment(sketch, "E415", {"start": v(6.69, 11.76) * mm, "end": v(6.71, 11.87) * mm});
            skLineSegment(sketch, "E416", {"start": v(6.71, 11.87) * mm, "end": v(6.98, 12.36) * mm});
            skLineSegment(sketch, "E417", {"start": v(6.98, 12.36) * mm, "end": v(7.08, 12.66) * mm});
            skLineSegment(sketch, "E418", {"start": v(7.08, 12.66) * mm, "end": v(7.2, 13.18) * mm});
            skLineSegment(sketch, "E419", {"start": v(7.2, 13.18) * mm, "end": v(7.25, 13.91) * mm});
            skSolve(sketch);
        }
        {
            var Q0;
            Q0=qSketchRegion(id+"F0",true);
            extrude(context, id + "F1", {"entities" : qUnion([Q0]), "depth" : 5 * mm, "offsetDistance" : 25 * mm});
        }
    });
